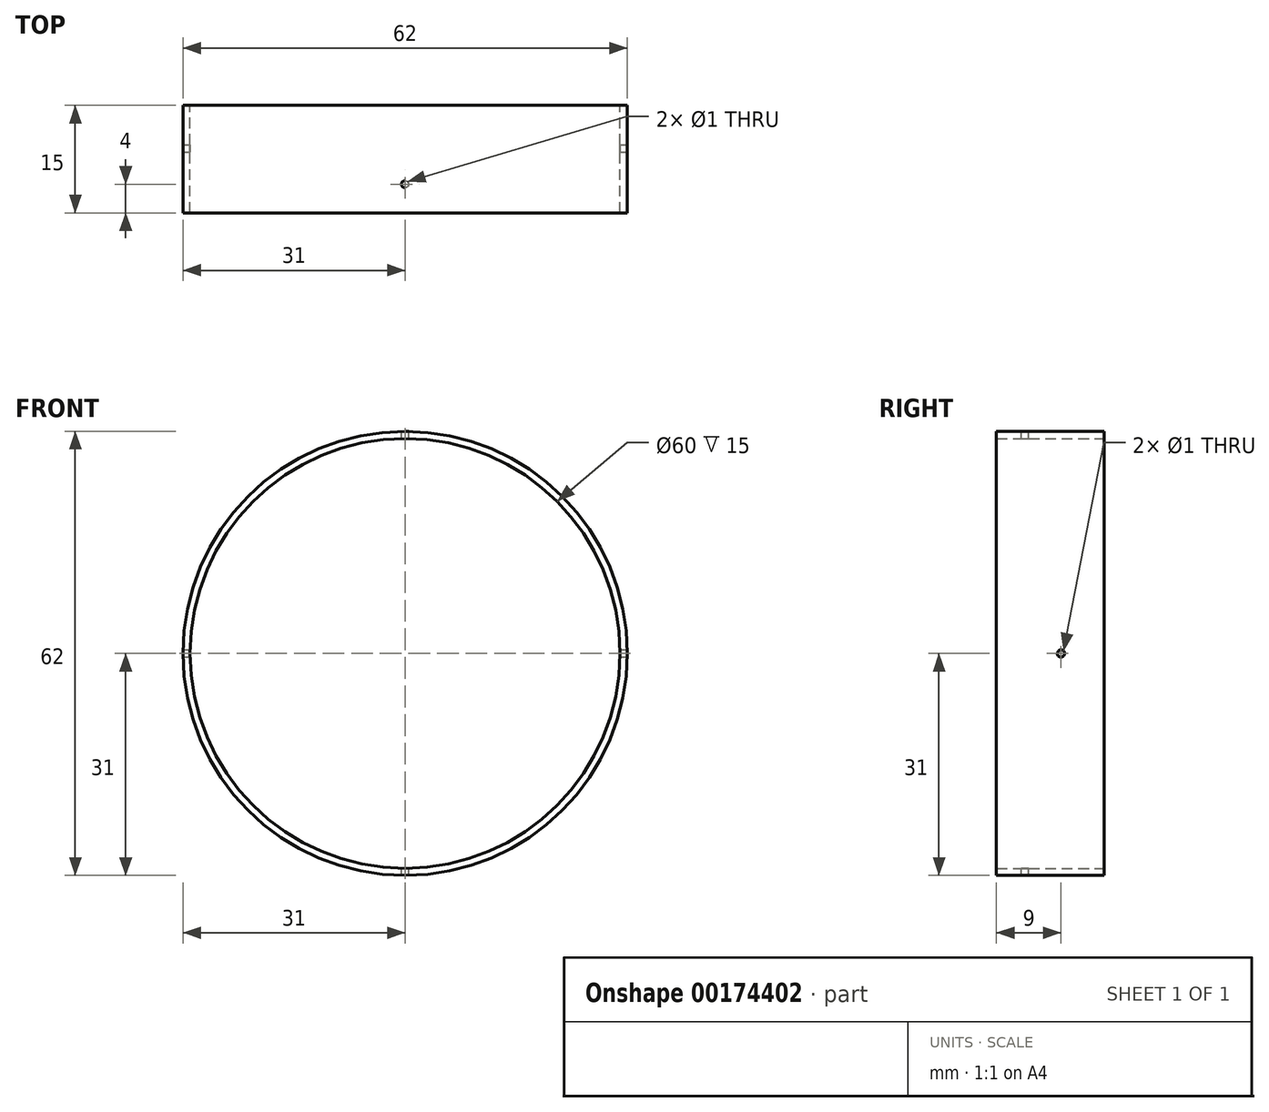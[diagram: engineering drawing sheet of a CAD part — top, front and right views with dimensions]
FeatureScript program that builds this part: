
annotation { "Feature Type Name" : "Feature", "Feature Type Description" : "" }
export const myFeature = defineFeature(function(context is Context, id is Id, definition is map)
    precondition{}
    {
        {
            var Q0;
            Q0=qCreatedBy(makeId("Right.planeOp"),FACE);
            var sketch = newSketch(context, id + "F0", { "sketchPlane" : qUnion([Q0])});
            skLineSegment(sketch, "E0", {"start": v(6, 31) * mm, "end": v(-9, 31) * mm});
            skLineSegment(sketch, "E1", {"start": v(-9, 31) * mm, "end": v(-9, 30) * mm});
            skLineSegment(sketch, "E2", {"start": v(-9, 30) * mm, "end": v(6, 30) * mm});
            skLineSegment(sketch, "E3", {"start": v(6, 30) * mm, "end": v(6, 31) * mm});
            skLineSegment(sketch, "E4", {"start": v(0, 30) * mm, "end": v(0, 0) * mm, "construction": true});
            skLineSegment(sketch, "E5", {"start": v(6, 30) * mm, "end": v(6, 0) * mm, "construction": true});
            skLineSegment(sketch, "E6", {"start": v(6, 0) * mm, "end": v(0, 0) * mm, "construction": true});
            skSolve(sketch);
        }
        {
            var Q0;
            Q0 = qSketchRegion(id + "F0", true);
            var Q1;
            Q1=sQuery(id+"F0.wireOp",EDGE,"E6");
            revolve(context, id + "F1", {"entities" : qUnion([Q0]), "axis" : qUnion([Q1]), "revolveType" : RevolveType.FULL});
        }
        {
            var Q0;
            Q0=qCreatedBy(makeId("Right.planeOp"),FACE);
            var sketch = newSketch(context, id + "F2", { "sketchPlane" : qUnion([Q0])});
            skCircle(sketch, "E7", {"center": v(0, 0) * mm, "radius": 0.5 * mm});
            skLineSegment(sketch, "E8.0", {"start": v(6, 31) * mm, "end": v(-9, 31) * mm, "construction": true});
            skLineSegment(sketch, "E8.2", {"start": v(-9, 30) * mm, "end": v(6, 30) * mm, "construction": true});
            skLineSegment(sketch, "E8.3", {"start": v(6, 30) * mm, "end": v(6, 31) * mm, "construction": true});
            skSolve(sketch);
        }
        {
            var Q0;
            Q0 = qSketchRegion(id + "F2", true);
            extrude(context, id + "F3", {"entities" : qUnion([Q0]), "operationType" : NewBodyOperationType.REMOVE, "endBound" : BoundingType.THROUGH_ALL, "oppositeDirection" : true, "depth" : 25 * mm, "hasSecondDirection" : true, "secondDirectionBound" : SecondDirectionBoundingType.THROUGH_ALL, "secondDirectionOppositeDirection" : false, "secondDirectionDepth" : 25 * mm});
        }
        {
            var Q0;
            Q0=qCreatedBy(makeId("Top.planeOp"),FACE);
            var sketch = newSketch(context, id + "F4", { "sketchPlane" : qUnion([Q0])});
            skCircle(sketch, "E9", {"center": v(0, -5) * mm, "radius": 0.5 * mm});
            skSolve(sketch);
        }
        {
            var Q0;
            Q0 = qSketchRegion(id + "F4", true);
            extrude(context, id + "F5", {"entities" : qUnion([Q0]), "operationType" : NewBodyOperationType.REMOVE, "endBound" : BoundingType.THROUGH_ALL, "oppositeDirection" : true, "depth" : 25 * mm, "hasSecondDirection" : true, "secondDirectionBound" : SecondDirectionBoundingType.THROUGH_ALL, "secondDirectionOppositeDirection" : false, "secondDirectionDepth" : 25 * mm});
        }
        {
            var Q0;
            Q0=qCreatedBy(makeId("Top.planeOp"),FACE);
            var sketch = newSketch(context, id + "F6", { "sketchPlane" : qUnion([Q0])});
            skLineSegment(sketch, "E10", {"start": v(0, 0) * mm, "end": v(-32.92, 0) * mm});
            skLineSegment(sketch, "E11", {"start": v(0, 0) * mm, "end": v(32.92, 0) * mm});
            skSolve(sketch);
        }
        {
            var Q0;
            Q0=qCreatedBy(makeId("Top.planeOp"),FACE);
            var Q1;
            Q1=sQuery(id+"F6.wireOp",EDGE,"E10");
            cPlane(context, id + "F7", {"entities" : qUnion([Q0, Q1]), "cplaneType" : CPlaneType.LINE_ANGLE, "offset" : 25 * mm, "angle" : 60 * degree, "width" : 150 * mm, "height" : 150 * mm});
        }
    });
